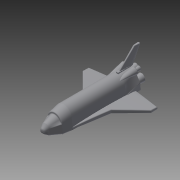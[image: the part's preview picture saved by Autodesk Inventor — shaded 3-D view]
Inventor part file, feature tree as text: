
AUTODESK INVENTOR PART (.ipt)
format: ipt  version: 2015 (Build 190159000, 159)  size: 1,976,320 bytes
history: native  units: in
note: dims shown in document units (in); Inventor stores cm internally (conversion verified against a paired STEP export)
features: sketch x28, plane x14, loft x11, extrude x8, fillet x6, other x3, projected_geometry x3, mirror x2, chamfer x2
ambient origin geometry x8: Origin, YZ Plane, XZ Plane, XY Plane, X Axis, Y Axis, Z Axis, Center Point
bodies: Solid1 (feature_tree)
feature tree (77):
  extrude  "Extrusion1"  TaperAngle=0.0deg  [1 undecoded]
  plane  "Work Plane1"
  plane  "Work Plane2"
  plane  "Work Plane3"
  loft  "Loft1"
  loft  "Loft2"
  fillet  "Fillet1"  Radius=240.6614in
  loft  "Loft4"
  fillet  "Fillet2"  Radius=125.0in
  extrude  "Extrusion2"  TaperAngle=0.0deg  [1 undecoded]
  extrude  "Extrusion3"  Depth=100.0in
  fillet  "Fillet3"  [1 undecoded]
  plane  "Work Plane4"
  mirror  "Mirror1"
  plane  "Work Plane5"
  sketch  "Sketch12"  dims[d36=0.0in d37=90.0deg d38=125.0in]
  loft  "Loft5"
  chamfer  "Chamfer1"  Angle=90.0deg  [1 undecoded]
  chamfer  "Chamfer2"  Angle=90.0deg  [1 undecoded]
  sketch  "Sketch15"  dims[d39=15.0in]
  plane  "Work Plane6"
  plane  "Work Plane7"
  loft  "Loft8"
  mirror  "Mirror2"
  extrude  "Extrusion5"  Depth=125.0in
  extrude  "Extrusion6"  TaperAngle=0.0deg  [1 undecoded]
  plane  "Work Plane8"
  sketch  "Sketch20"  dims[d51=10.0in]
  plane  "Work Plane10"
  loft  "Loft9"
  fillet  "Fillet4"  Radius=84.0in
  extrude  "Extrusion7"  Depth=0.6803in
  fillet  "Fillet5"  Radius=48.0in
  fillet  "Fillet6"  Radius=6500.0in
  sketch  "Sketch23"  dims[d55=0.0in]
  plane  "Work Plane11"
  sketch  "Sketch24"  dims[d56=0.0in]
  loft  "Loft10"
  loft  "Loft11"
  sketch  "Sketch27"  dims[d64=60.0in d70=125.0in]
  plane  "Work Plane12"
  loft  "Loft12"
  loft  "Loft13"
  loft  "Loft14"
  sketch  "Sketch31"  dims[d89=6500.0in d90=7700.0in]
  plane  "Work Plane13"
  sketch  "Sketch32"  dims[d91=10.0in d92=345.0in d93=0.0in]
  sketch  "Sketch33"  dims[d94=10.0in d95=125.0in]
  plane  "Work Plane14"
  extrude  "Extrusion8"  Depth=245.0in
  sketch  "Sketch35"  dims[d98=10.0in d99=0.0in]
  plane  "Work Plane15"
  extrude  "Extrusion9"  Depth=90.0in
  sketch  "Sketch1"  dims[d5=250.0in d12=0.0in]
  sketch  "Sketch2"  dims[d13=75.0in d15=110.0in]
  other  "Edges1"
  sketch  "Sketch3"  dims[d21=98.0in d24=110.0in d25=240.6614in]
  sketch  "Sketch6"  dims[d26=730.0in d27=0.0in d28=300.0in d29=125.0in]
  sketch  "Sketch7"  dims[d30=250.0in d31=0.0in]
  other  "Edges3"
  sketch  "Sketch8"  dims[d32=125.0in d33=100.0in d34=0.0in d35=90.0deg]
  other  "Edges4"
  sketch  "Sketch17"  dims[d40=20.0in]
  sketch  "Sketch18"  dims[d41=10.0in]
  sketch  "Sketch19"  dims[d50=15.0in]
  projected_geometry  "Projected Loop7"
  sketch  "Sketch21"  dims[d52=75.0in]
  sketch  "Sketch22"  dims[d54=125.0in]
  sketch  "Sketch25"  dims[d57=0.0in d58=0.0in d59=90.0deg d60=0.0in d61=90.0deg]
  sketch  "Sketch26"  dims[d62=10.65in d63=50.0in]
  sketch  "Sketch28"  dims[d71=50.0in d72=0.0in d73=90.0deg]
  sketch  "Sketch29"  dims[d74=0.0in d75=90.0deg d76=40.0in d79=84.0in]
  sketch  "Sketch30"  dims[d80=0.0in d82=0.6803in d83=48.0in d84=0.0in d85=6500.0in]
  sketch  "Sketch34"  dims[d96=200.0in d97=0.0in]
  projected_geometry  "Projected Loop8"
  projected_geometry  "Projected Loop9"
  sketch  "Sketch36"  dims[d100=0.0in d101=245.0in d102=90.0in d105=15.0in d106=0.0618in d107=45.0deg d108=345.0in d109=0.0in d110=90.0deg d111=0.0in d112=90.0deg d113=5.2in d114=0.125in d115=45.0deg d116=5.2in d117=0.125in d118=45.0deg d119=-200.0in d126=100.0in d127=25.0in d133=-205.0in d134=50.0in d135=60.0in d137=0.0in d138=90.0deg d139=0.0in d140=90.0deg d141=160.0in d142=100.0in d143=0.6528in d144=0.0in d145=0.0in d146=9000.0in d147=0.0in d148=15.0in d149=25.0in d150=0.0in d151=30.0in d152=0.0in d153=-20.0in d154=30.0in d155=10.0in d156=1.2162in d157=1.2162in d158=195.0in d160=225.0in d166=30.0in d167=225.0in d168=20.0in d169=30.0in d170=20.0in d171=80.0in d172=0.0in d173=90.0deg d174=0.0in d175=90.0deg d176=7.0in d177=0.1374in d178=200.0in d179=0.0in d180=9.475in d184=150.0in d185=150.0in d186=9.475in d187=40.0in d188=80.0in d189=65.0in d190=60.0in d191=20.0in d192=125.0in d193=0.0in d194=13.0in d195=32.0in d196=55.0in d197=55.0in d198=55.0in d199=80.0in d200=95.0in d201=95.0in d202=40.0in d203=0.0in d204=90.0deg d205=0.0in d206=90.0deg d207=0.0in d208=90.0deg d209=0.0in d210=90.0deg d211=25.0in d212=90.0in d213=8.0in d214=0.0in d215=90.0deg d216=0.0in d217=90.0deg d218=105.0in d219=5.0in d220=5.0in d221=0.0in d222=90.0deg d223=0.0in d224=90.0deg d225=105.0in d226=5.0in d227=5.0in d228=0.0in d229=90.0deg d230=0.0in d231=90.0deg d232=-20.0in d233=90.0deg d234=95.0in d235=0.0in d236=90.0deg d237=105.0in d238=0.0in]
note: 6 required parameter values undecoded (feature->parameter linkage not recoverable at this tier; creation-order binding heuristic only, values carry confidence <= 0.55)
